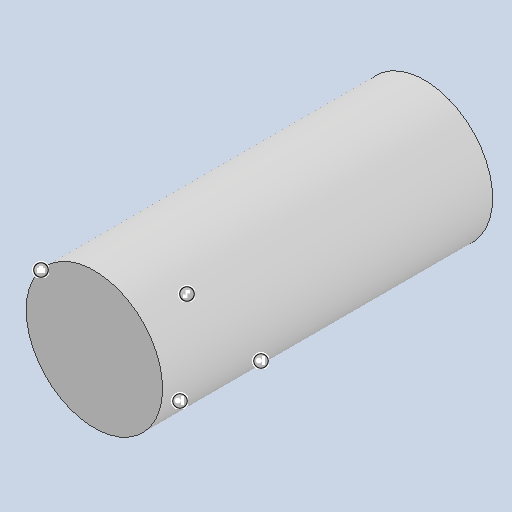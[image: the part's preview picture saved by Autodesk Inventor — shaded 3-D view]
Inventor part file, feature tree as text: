
AUTODESK INVENTOR PART (.ipt)
format: ipt  version: 2023.4 (Build 274418000, 418)  size: 100,352 bytes
history: native  units: mm
features: extrude x1
ambient origin geometry x8: Origin, YZ Plane, XZ Plane, XY Plane, X Axis, Y Axis, Z Axis, Center Point
bodies: Solid1 (feature_tree)
feature tree (1):
  extrude  "Extrusion1"  TaperAngle=0.0deg  [1 undecoded]
note: 1 required parameter value undecoded (feature->parameter linkage not recoverable at this tier; creation-order binding heuristic only, values carry confidence <= 0.55)
